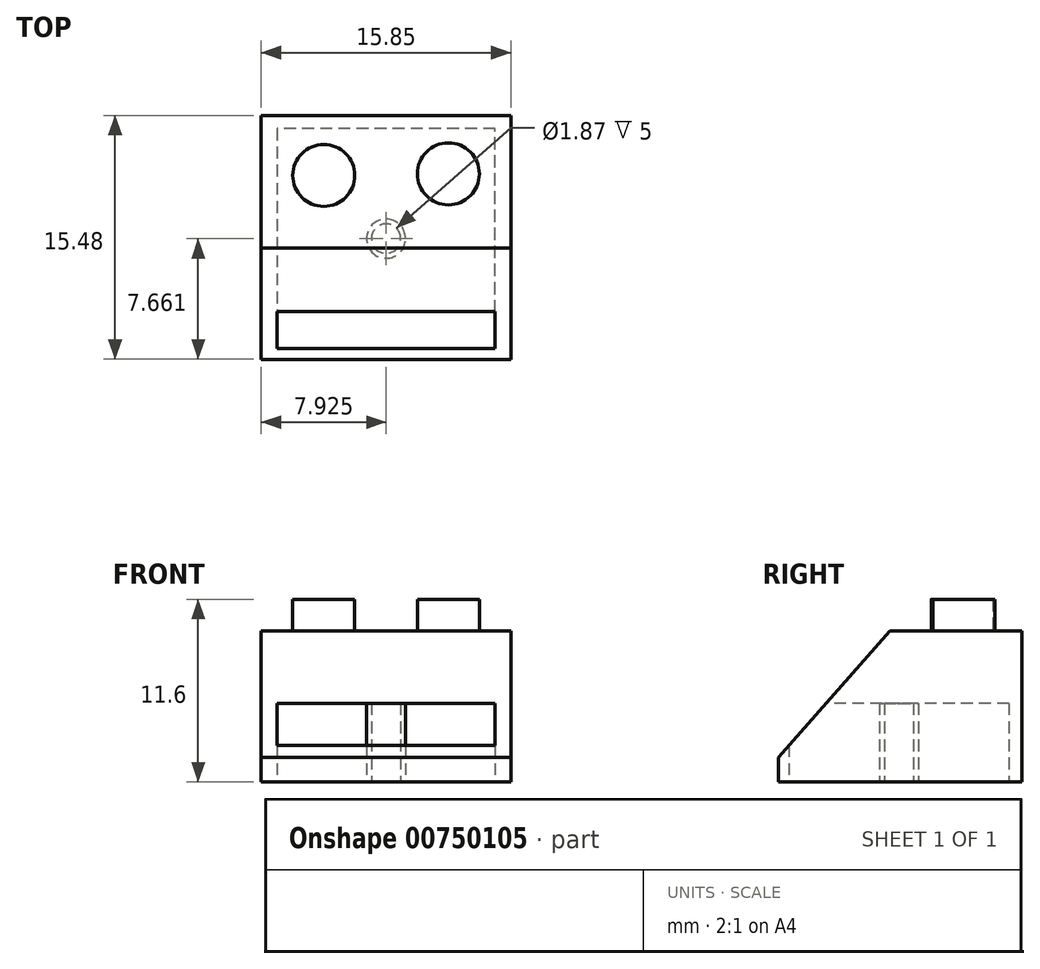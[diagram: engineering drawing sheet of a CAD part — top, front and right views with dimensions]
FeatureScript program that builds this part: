
annotation { "Feature Type Name" : "Feature", "Feature Type Description" : "" }
export const myFeature = defineFeature(function(context is Context, id is Id, definition is map)
    precondition{}
    {
        {
            var Q0;
            Q0=qCreatedBy(makeId("Right.planeOp"),FACE);
            var sketch = newSketch(context, id + "F0", { "sketchPlane" : qUnion([Q0])});
            skLineSegment(sketch, "E0", {"start": v(-17.25, 47.73) * mm, "end": v(-17.25, 38.13) * mm});
            skLineSegment(sketch, "E1", {"start": v(-17.25, 38.13) * mm, "end": v(-32.73, 38.13) * mm});
            skLineSegment(sketch, "E2", {"start": v(-32.73, 38.13) * mm, "end": v(-32.73, 39.7) * mm});
            skLineSegment(sketch, "E3", {"start": v(-17.25, 47.73) * mm, "end": v(-25.65, 47.73) * mm});
            skLineSegment(sketch, "E4", {"start": v(-25.65, 47.73) * mm, "end": v(-32.73, 39.7) * mm});
            skSolve(sketch);
        }
        {
            var Q0;
            Q0 = qSketchRegion(id + "F0", true);
            extrude(context, id + "F1", {"entities" : qUnion([Q0]), "depth" : 15.85 * mm, "offsetDistance" : 25 * mm});
        }
        {
            var Q0;
            Q0=makeQuery(id+"F1.opExtrude","SWEPT_FACE",FACE,{"disambiguationData":[OSD([sQuery(id+"F0.wireOp",EDGE,"E3")])]});
            var sketch = newSketch(context, id + "F2", { "sketchPlane" : qUnion([Q0])});
            skCircle(sketch, "E5", {"center": v(3.97, -21.05) * mm, "radius": 1.97 * mm});
            skCircle(sketch, "E6", {"center": v(11.88, -20.95) * mm, "radius": 1.97 * mm});
            skSolve(sketch);
        }
        {
            var Q0;
            Q0 = qSketchRegion(id + "F2", true);
            extrude(context, id + "F3", {"entities" : qUnion([Q0]), "operationType" : NewBodyOperationType.ADD, "depth" : 2 * mm, "offsetDistance" : 25 * mm});
        }
        {
            var Q0;
            Q0=makeQuery(id+"F1.opExtrude","SWEPT_FACE",FACE,{"disambiguationData":[OSD([sQuery(id+"F0.wireOp",EDGE,"E1")])]});
            var sketch = newSketch(context, id + "F4", { "sketchPlane" : qUnion([Q0])});
            skLineSegment(sketch, "E7", {"start": v(1, 32.06) * mm, "end": v(14.85, 32.06) * mm});
            skLineSegment(sketch, "E8", {"start": v(14.85, 32.06) * mm, "end": v(14.85, 21.55) * mm});
            skLineSegment(sketch, "E9", {"start": v(14.85, 21.55) * mm, "end": v(14.85, 18.08) * mm});
            skLineSegment(sketch, "E10", {"start": v(14.85, 18.08) * mm, "end": v(1, 18.08) * mm});
            skLineSegment(sketch, "E11", {"start": v(1, 18.08) * mm, "end": v(1, 32.06) * mm});
            skLineSegment(sketch, "E12", {"start": v(1, 32.06) * mm, "end": v(14.85, 18.08) * mm});
            skLineSegment(sketch, "E13", {"start": v(14.85, 32.06) * mm, "end": v(1, 18.08) * mm});
            skCircle(sketch, "E14", {"center": v(7.92, 25.07) * mm, "radius": 1.24 * mm});
            skCircle(sketch, "E15", {"center": v(7.92, 25.07) * mm, "radius": 0.93 * mm});
            skSolve(sketch);
        }
        {
            var Q0;
            Q0 = qSketchRegion(id + "F4", true);
            var Q1;
            {var subQ0=sQuery(id+"F4.wireOp",EDGE,"E13");var subQ1=sQuery(id+"F4.wireOp",EDGE,"E12");var subQ2=makeQuery(id+"F4.imprint","INTERSECT",VERTEX,{"derivedFrom":[subQ1,subQ0]});Q1=makeQuery(id+"F4.imprint","IMPRINT",FACE,{"disambiguationData":[TD([[makeQuery(id+"F4.imprint","IMPRINT",EDGE,{"disambiguationData":[TD([[subQ2,-1.0]])],"derivedFrom":subQ1}),-1.0]])]});}
            var Q2;
            {var subQ0=sQuery(id+"F4.wireOp",EDGE,"E15");var subQ1=sQuery(id+"F4.wireOp",EDGE,"E12");var subQ2=makeQuery(id+"F4.imprint","INTERSECT",VERTEX,{"disambiguationData":[OD(0.0)],"derivedFrom":[subQ1,subQ0]});Q2=makeQuery(id+"F4.imprint","IMPRINT",FACE,{"disambiguationData":[TD([[makeQuery(id+"F4.imprint","IMPRINT",EDGE,{"disambiguationData":[TD([[subQ2,-1.0]])],"derivedFrom":subQ1}),-1.0]])]});}
            var Q3;
            {var subQ0=sQuery(id+"F4.wireOp",EDGE,"E15");var subQ1=sQuery(id+"F4.wireOp",EDGE,"E12");var subQ2=makeQuery(id+"F4.imprint","INTERSECT",VERTEX,{"disambiguationData":[OD(0.0)],"derivedFrom":[subQ1,subQ0]});Q3=makeQuery(id+"F4.imprint","IMPRINT",FACE,{"disambiguationData":[TD([[makeQuery(id+"F4.imprint","IMPRINT",EDGE,{"disambiguationData":[TD([[subQ2,-1.0]])],"derivedFrom":subQ1}),1.0]])]});}
            var Q4;
            {var subQ0=sQuery(id+"F4.wireOp",EDGE,"E13");var subQ1=sQuery(id+"F4.wireOp",EDGE,"E12");var subQ2=makeQuery(id+"F4.imprint","INTERSECT",VERTEX,{"derivedFrom":[subQ1,subQ0]});Q4=makeQuery(id+"F4.imprint","IMPRINT",FACE,{"disambiguationData":[TD([[makeQuery(id+"F4.imprint","IMPRINT",EDGE,{"disambiguationData":[TD([[subQ2,-1.0]])],"derivedFrom":subQ1}),1.0]])]});}
            extrude(context, id + "F5", {"entities" : qUnion([Q0, Q1, Q2, Q3, Q4]), "operationType" : NewBodyOperationType.REMOVE, "oppositeDirection" : true, "depth" : 5 * mm, "offsetDistance" : 25 * mm});
        }
    });
